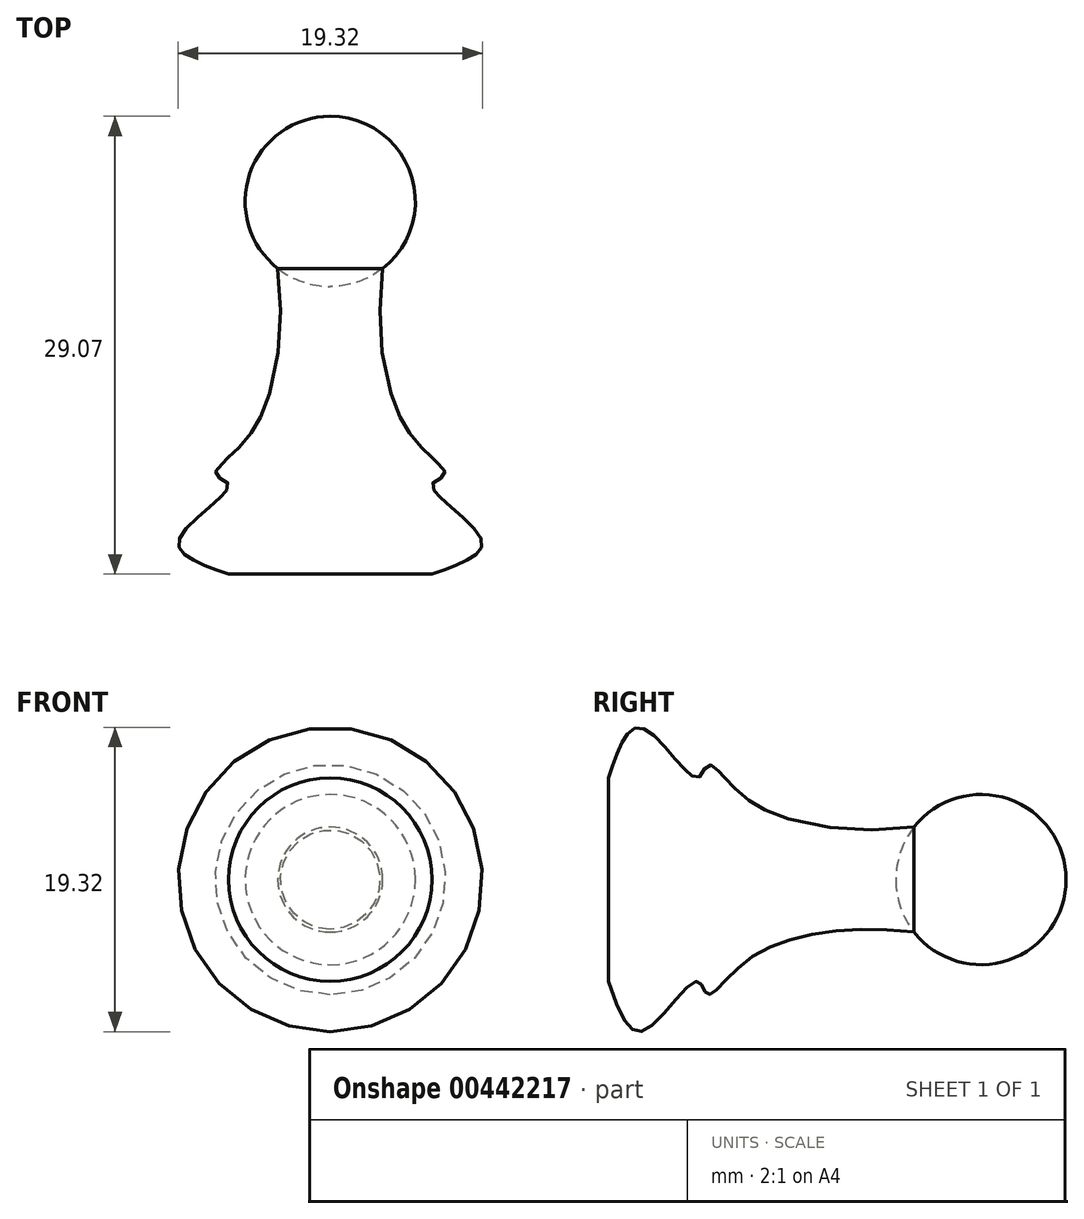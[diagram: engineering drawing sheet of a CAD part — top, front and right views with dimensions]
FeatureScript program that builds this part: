
annotation { "Feature Type Name" : "Feature", "Feature Type Description" : "" }
export const myFeature = defineFeature(function(context is Context, id is Id, definition is map)
    precondition{}
    {
        {
            var Q0;
            Q0=qCreatedBy(makeId("Top.planeOp"),FACE);
            var sketch = newSketch(context, id + "F0", { "sketchPlane" : qUnion([Q0])});
            skLineSegment(sketch, "E0", {"start": v(0, 0) * mm, "end": v(0, 25.52) * mm});
            skLineSegment(sketch, "E1", {"start": v(0, 0) * mm, "end": v(6.46, 0) * mm});
            skFitSpline(sketch, "E2", {"points": [v(6.46, 0) * mm, v(9.53, 2.38) * mm, v(6.46, 5.66) * mm, v(7.29, 6.29) * mm, v(5.18, 8.75) * mm, v(3.33, 19.41) * mm], "startDerivative": vector(37.6, 12.71) * mm, "endDerivative": vector(4.56, 39.56) * mm});
            skCircle(sketch, "E3", {"center": v(0, 23.67) * mm, "radius": 5.4 * mm});
            skLineSegment(sketch, "E4", {"start": v(3.33, 19.41) * mm, "end": v(0, 19.41) * mm});
            skLineSegment(sketch, "E5", {"start": v(0, 25.52) * mm, "end": v(0, 29.07) * mm});
            skSolve(sketch);
        }
        {
            var Q0;
            {var subQ6=sQuery(id+"F0.wireOp",EDGE,"E1");Q0=makeQuery(id+"F0.imprint","IMPRINT",FACE,{"disambiguationData":[TD([[makeQuery(id+"F0.imprint","IMPRINT",EDGE,{"derivedFrom":subQ6}),1.0]])]});}
            var Q1;
            {var subQ0=sQuery(id+"F0.wireOp",EDGE,"E5");Q1=makeQuery(id+"F0.imprint","IMPRINT",FACE,{"disambiguationData":[TD([[makeQuery(id+"F0.imprint","IMPRINT",EDGE,{"derivedFrom":subQ0}),-1.0]])]});}
            var Q2;
            Q2=sQuery(id+"F0.wireOp",EDGE,"E0");
            revolve(context, id + "F1", {"entities" : qUnion([Q0, Q1]), "axis" : qUnion([Q2]), "revolveType" : RevolveType.FULL});
        }
    });
